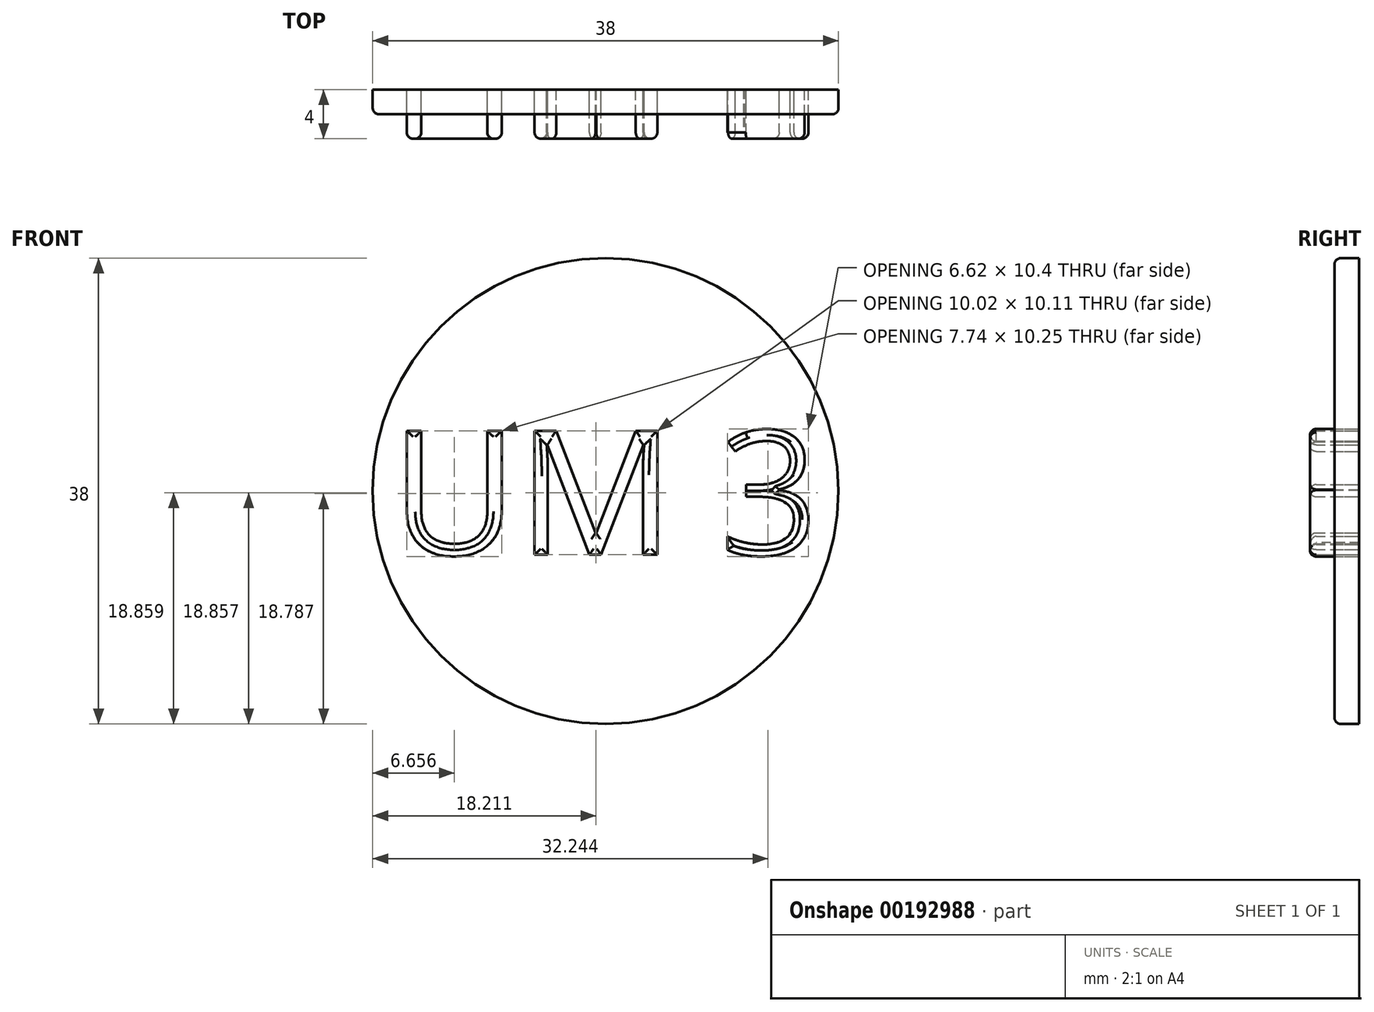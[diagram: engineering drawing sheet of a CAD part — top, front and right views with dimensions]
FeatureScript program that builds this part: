
annotation { "Feature Type Name" : "Feature", "Feature Type Description" : "" }
export const myFeature = defineFeature(function(context is Context, id is Id, definition is map)
    precondition{}
    {
        {
            var Q0;
            Q0=qCreatedBy(makeId("Front.planeOp"),FACE);
            var sketch = newSketch(context, id + "F0", { "sketchPlane" : qUnion([Q0])});
            skCircle(sketch, "E0", {"center": v(0, 0) * mm, "radius": 19 * mm});
            skText(sketch, "E1", { "text": "UM 3", "fontName": "OpenSans-Regular.ttf"});
            const initialGuessF0  = {"E1": [-0.0175, -0.0052, 1, 0, 0.0102]};
            skSetInitialGuess(sketch, initialGuessF0);
            skSolve(sketch);
        }
        {
            var Q0;
            Q0=makeQuery(id+"F0.imprint","IMPRINT",FACE,{"disambiguationData":[TD([[makeQuery(id+"F0.imprint","IMPRINT",EDGE,{"derivedFrom":sQuery(id+"F0.wireOp",EDGE,"E1.sketch_text.stroke-32")}),-1.0]])]});
            var Q1;
            Q1=makeQuery(id+"F0.imprint","IMPRINT",FACE,{"disambiguationData":[TD([[makeQuery(id+"F0.imprint","IMPRINT",EDGE,{"derivedFrom":sQuery(id+"F0.wireOp",EDGE,"E1.sketch_text.stroke-14")}),-1.0]])]});
            var Q2;
            Q2=makeQuery(id+"F0.imprint","IMPRINT",FACE,{"disambiguationData":[TD([[makeQuery(id+"F0.imprint","IMPRINT",EDGE,{"derivedFrom":sQuery(id+"F0.wireOp",EDGE,"E1.sketch_text.stroke-0")}),-1.0]])]});
            extrude(context, id + "F1", {"entities" : qUnion([Q0, Q1, Q2]), "depth" : 4 * mm});
        }
        {
            var Q0;
            Q0=makeQuery(id+"F0.imprint","IMPRINT",FACE,{"disambiguationData":[TD([[makeQuery(id+"F0.imprint","IMPRINT",EDGE,{"derivedFrom":sQuery(id+"F0.wireOp",EDGE,"E0")}),1.0]])]});
            extrude(context, id + "F2", {"entities" : qUnion([Q0]), "depth" : 2 * mm});
        }
        {
            var Q0;
            Q0=makeQuery(id+"F1.opExtrude","CAP_FACE",FACE,{"disambiguationData":[OSD([sQuery(id+"F0.wireOp",EDGE,"E1.sketch_text.stroke-0"),sQuery(id+"F0.wireOp",EDGE,"E1.sketch_text.stroke-1"),sQuery(id+"F0.wireOp",EDGE,"E1.sketch_text.stroke-2"),sQuery(id+"F0.wireOp",EDGE,"E1.sketch_text.stroke-3"),sQuery(id+"F0.wireOp",EDGE,"E1.sketch_text.stroke-4"),sQuery(id+"F0.wireOp",EDGE,"E1.sketch_text.stroke-5"),sQuery(id+"F0.wireOp",EDGE,"E1.sketch_text.stroke-6"),sQuery(id+"F0.wireOp",EDGE,"E1.sketch_text.stroke-7"),sQuery(id+"F0.wireOp",EDGE,"E1.sketch_text.stroke-8"),sQuery(id+"F0.wireOp",EDGE,"E1.sketch_text.stroke-9"),sQuery(id+"F0.wireOp",EDGE,"E1.sketch_text.stroke-10"),sQuery(id+"F0.wireOp",EDGE,"E1.sketch_text.stroke-11"),sQuery(id+"F0.wireOp",EDGE,"E1.sketch_text.stroke-12"),sQuery(id+"F0.wireOp",EDGE,"E1.sketch_text.stroke-13")])],"isStart":false});
            var Q1;
            Q1=makeQuery(id+"F1.opExtrude","CAP_FACE",FACE,{"disambiguationData":[OSD([sQuery(id+"F0.wireOp",EDGE,"E1.sketch_text.stroke-14"),sQuery(id+"F0.wireOp",EDGE,"E1.sketch_text.stroke-15"),sQuery(id+"F0.wireOp",EDGE,"E1.sketch_text.stroke-16"),sQuery(id+"F0.wireOp",EDGE,"E1.sketch_text.stroke-17"),sQuery(id+"F0.wireOp",EDGE,"E1.sketch_text.stroke-18"),sQuery(id+"F0.wireOp",EDGE,"E1.sketch_text.stroke-19"),sQuery(id+"F0.wireOp",EDGE,"E1.sketch_text.stroke-20"),sQuery(id+"F0.wireOp",EDGE,"E1.sketch_text.stroke-21"),sQuery(id+"F0.wireOp",EDGE,"E1.sketch_text.stroke-22"),sQuery(id+"F0.wireOp",EDGE,"E1.sketch_text.stroke-23"),sQuery(id+"F0.wireOp",EDGE,"E1.sketch_text.stroke-24"),sQuery(id+"F0.wireOp",EDGE,"E1.sketch_text.stroke-25"),sQuery(id+"F0.wireOp",EDGE,"E1.sketch_text.stroke-26"),sQuery(id+"F0.wireOp",EDGE,"E1.sketch_text.stroke-27"),sQuery(id+"F0.wireOp",EDGE,"E1.sketch_text.stroke-28"),sQuery(id+"F0.wireOp",EDGE,"E1.sketch_text.stroke-29"),sQuery(id+"F0.wireOp",EDGE,"E1.sketch_text.stroke-30"),sQuery(id+"F0.wireOp",EDGE,"E1.sketch_text.stroke-31")])],"isStart":false});
            var Q2;
            Q2=makeQuery(id+"F1.opExtrude","CAP_FACE",FACE,{"disambiguationData":[OSD([sQuery(id+"F0.wireOp",EDGE,"E1.sketch_text.stroke-32"),sQuery(id+"F0.wireOp",EDGE,"E1.sketch_text.stroke-33"),sQuery(id+"F0.wireOp",EDGE,"E1.sketch_text.stroke-34"),sQuery(id+"F0.wireOp",EDGE,"E1.sketch_text.stroke-35"),sQuery(id+"F0.wireOp",EDGE,"E1.sketch_text.stroke-36"),sQuery(id+"F0.wireOp",EDGE,"E1.sketch_text.stroke-37"),sQuery(id+"F0.wireOp",EDGE,"E1.sketch_text.stroke-38"),sQuery(id+"F0.wireOp",EDGE,"E1.sketch_text.stroke-39"),sQuery(id+"F0.wireOp",EDGE,"E1.sketch_text.stroke-40"),sQuery(id+"F0.wireOp",EDGE,"E1.sketch_text.stroke-41"),sQuery(id+"F0.wireOp",EDGE,"E1.sketch_text.stroke-42"),sQuery(id+"F0.wireOp",EDGE,"E1.sketch_text.stroke-43"),sQuery(id+"F0.wireOp",EDGE,"E1.sketch_text.stroke-44"),sQuery(id+"F0.wireOp",EDGE,"E1.sketch_text.stroke-45"),sQuery(id+"F0.wireOp",EDGE,"E1.sketch_text.stroke-46"),sQuery(id+"F0.wireOp",EDGE,"E1.sketch_text.stroke-47"),sQuery(id+"F0.wireOp",EDGE,"E1.sketch_text.stroke-48"),sQuery(id+"F0.wireOp",EDGE,"E1.sketch_text.stroke-49"),sQuery(id+"F0.wireOp",EDGE,"E1.sketch_text.stroke-50"),sQuery(id+"F0.wireOp",EDGE,"E1.sketch_text.stroke-51"),sQuery(id+"F0.wireOp",EDGE,"E1.sketch_text.stroke-52"),sQuery(id+"F0.wireOp",EDGE,"E1.sketch_text.stroke-53"),sQuery(id+"F0.wireOp",EDGE,"E1.sketch_text.stroke-54"),sQuery(id+"F0.wireOp",EDGE,"E1.sketch_text.stroke-55"),sQuery(id+"F0.wireOp",EDGE,"E1.sketch_text.stroke-56"),sQuery(id+"F0.wireOp",EDGE,"E1.sketch_text.stroke-57"),sQuery(id+"F0.wireOp",EDGE,"E1.sketch_text.stroke-58"),sQuery(id+"F0.wireOp",EDGE,"E1.sketch_text.stroke-59")])],"isStart":false});
            fillet(context, id + "F3", {"entities" : qUnion([Q0, Q1, Q2]), "radius" : 0.5 * mm, "tangentPropagation" : true, "allowEdgeOverflow" : false});
        }
        {
            var Q0;
            Q0=makeQuery(id+"F2.opExtrude","CAP_EDGE",EDGE,{"disambiguationData":[OSD([sQuery(id+"F0.wireOp",EDGE,"E0")])],"isStart":false});
            fillet(context, id + "F4", {"entities" : qUnion([Q0]), "radius" : 0.5 * mm, "tangentPropagation" : true, "allowEdgeOverflow" : false});
        }
    });
